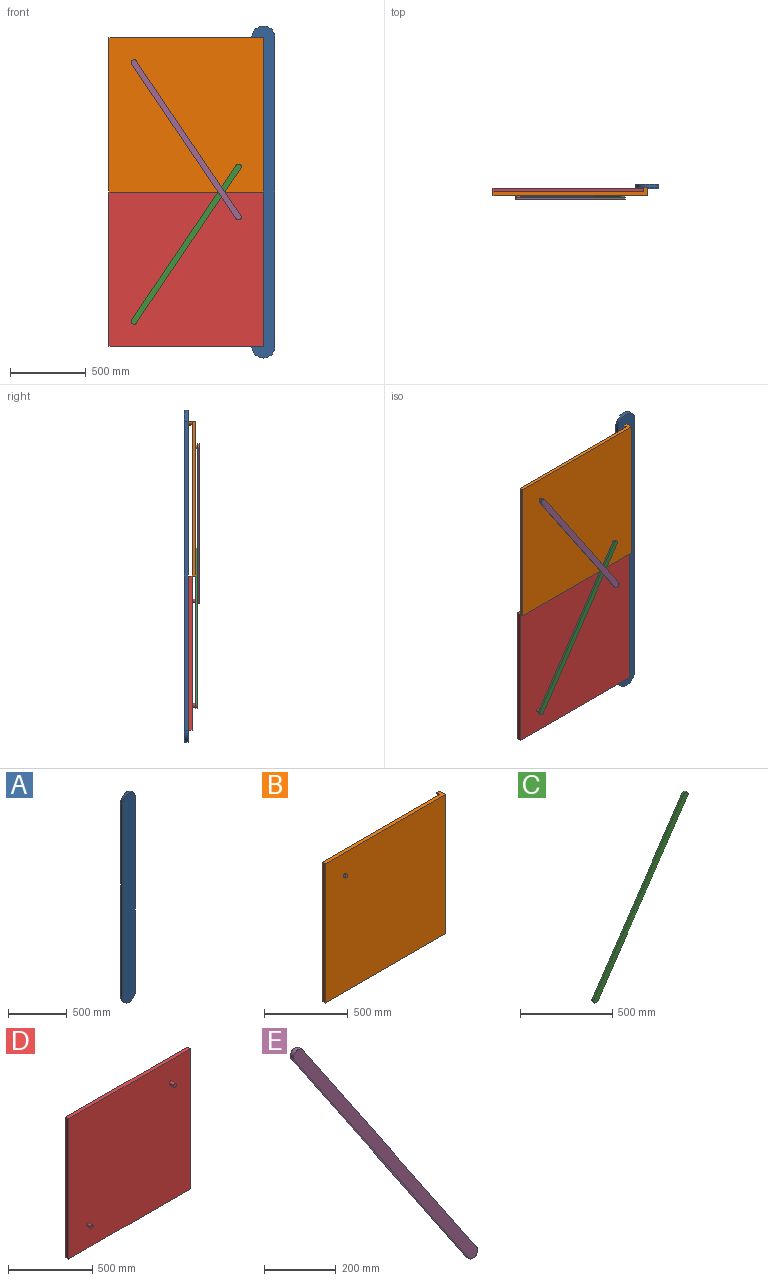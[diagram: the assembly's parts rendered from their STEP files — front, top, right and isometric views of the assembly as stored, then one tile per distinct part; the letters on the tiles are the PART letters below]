
ASSEMBLY  parts=5 mates=6
PART A: 6 faces, bbox 152.4x25.4x2184.4 mm
  f0: plane 2184.4x152.4mm, normal (0,-1,0), area 327918.3mm2, adj f1,f2,f3,f4
  f1: plane 2032x25.4mm, normal (1,0,0), area 51612.8mm2, adj f0,f2,f4,f5
  f2: cylinder r=76.2mm len=152.4mm, axis (0,-1,0), area 6080.5mm2, adj f0,f1,f3,f5
  f3: plane 2032x25.4mm, normal (-1,0,0), area 51612.8mm2, adj f0,f2,f4,f5
  f4: cylinder r=76.2mm len=152.4mm, axis (0,-1,0), area 6080.5mm2, adj f0,f1,f3,f5
  f5: plane 2184.4x152.4mm, normal (0,1,0), area 327918.3mm2, adj f1,f2,f3,f4
PART B: 10 faces, bbox 1016x63.5x1016 mm
  f0: plane 1016x50.8mm, normal (0,0,1), area 26451.6mm2, adj f1,f3,f4,f5,f8,f9
  f1: plane 1016x25.4mm, normal (-1,0,0), area 25806.4mm2, adj f0,f2,f4,f5
  f2: plane 1016x25.4mm, normal (0,0,-1), area 25806.4mm2, adj f1,f3,f4,f5
  f3: plane 1016x50.8mm, normal (1,0,0), area 26451.6mm2, adj f0,f2,f4,f5,f8,f9
  f4: plane 1016x1016mm, normal (0,1,0), area 1031749.3mm2, adj f0,f1,f2,f3,f9
  f5: plane 1016x1016mm, normal (0,-1,0), area 1031749.3mm2, adj f0,f1,f2,f3,f7
  f6: plane 25.4x25.4mm, normal (0,-1,0), area 506.7mm2, adj f7
  f7: cylinder r=12.7mm len=25.4mm, axis (0,-1,0), area 1013.4mm2, adj f5,f6
  f8: plane 25.4x25.4mm, normal (0,1,0), area 506.7mm2, adj f0,f3,f9
  f9: cylinder r=25.4mm len=25.4mm, axis (0,-1,0), area 1013.4mm2, adj f0,f3,f4,f8
PART C: 6 faces, bbox 724.5x12.7x1054.1 mm
  f0: plane 1016x686.38mm, normal (-0.83,0,0.56), area 15571.7mm2, adj f1,f3,f4,f5
  f1: cylinder r=19.05mm len=34.84mm, axis (0,1,0), area 760.1mm2, adj f0,f2,f4,f5
  f2: plane 1016x686.38mm, normal (0.83,0,-0.56), area 15571.7mm2, adj f1,f3,f4,f5
  f3: cylinder r=19.05mm len=34.84mm, axis (0,1,0), area 760.1mm2, adj f0,f2,f4,f5
  f4: plane 1054.1x724.48mm, normal (0,-1,0), area 47855.3mm2, adj f0,f1,f2,f3
  f5: plane 1054.1x724.48mm, normal (0,1,0), area 47855.3mm2, adj f0,f1,f2,f3
PART D: 10 faces, bbox 1016x63.5x1016 mm
  f0: plane 1016x1016mm, normal (0,-1,0), area 1031242.6mm2, adj f1,f2,f3,f4,f7,f9
  f1: plane 1016x25.4mm, normal (0,0,1), area 25806.4mm2, adj f0,f2,f4,f5
  f2: plane 1016x25.4mm, normal (-1,0,0), area 25806.4mm2, adj f0,f1,f3,f5
  f3: plane 1016x25.4mm, normal (0,0,-1), area 25806.4mm2, adj f0,f2,f4,f5
  f4: plane 1016x25.4mm, normal (1,0,0), area 25806.4mm2, adj f0,f1,f3,f5
  f5: plane 1016x1016mm, normal (0,1,0), area 1032256mm2, adj f1,f2,f3,f4
  f6: plane 25.4x25.4mm, normal (0,-1,0), area 506.7mm2, adj f7
  f7: cylinder r=12.7mm len=25.4mm, axis (0,-1,0), area 2026.8mm2, adj f0,f6
  f8: plane 25.4x25.4mm, normal (0,-1,0), area 506.7mm2, adj f9
  f9: cylinder r=12.7mm len=38.1mm, axis (0,-1,0), area 3040.2mm2, adj f0,f8
PART E: 6 faces, bbox 724.5x12.7x1054.1 mm
  f0: plane 1054.1x724.48mm, normal (0,1,0), area 47855.3mm2, adj f1,f2,f3,f4
  f1: cylinder r=19.05mm len=34.84mm, axis (0,1,0), area 760.1mm2, adj f0,f2,f4,f5
  f2: plane 1016x686.38mm, normal (-0.83,0,-0.56), area 15571.7mm2, adj f0,f1,f3,f5
  f3: cylinder r=19.05mm len=34.84mm, axis (0,1,0), area 760.1mm2, adj f0,f2,f4,f5
  f4: plane 1016x686.38mm, normal (0.83,0,0.56), area 15571.7mm2, adj f0,f1,f3,f5
  f5: plane 1054.1x724.48mm, normal (0,-1,0), area 47855.3mm2, adj f1,f2,f3,f4
PLACE A at identity fixed
PLACE B at identity
PLACE C at identity
PLACE D at identity
PLACE E at identity
MATE revolute B.f5 <-> C.f3  axis (0,-1,0) through (343.19,0,164.81)mm
MATE revolute D.f5 <-> A.f4  axis (0,1,0) through (508,50.8,-1016)mm
MATE revolute E.f3 <-> D.f9  axis (0,1,0) through (343.19,-12.7,-164.81)mm
MATE revolute D.f7 <-> C.f1  axis (0,-1,0) through (-343.19,0,-851.19)mm
MATE revolute A.f2 <-> B.f9  axis (0,-1,0) through (508,50.8,1016)mm
MATE revolute B.f7 <-> E.f1  axis (0,-1,0) through (-343.19,-12.7,851.19)mm
